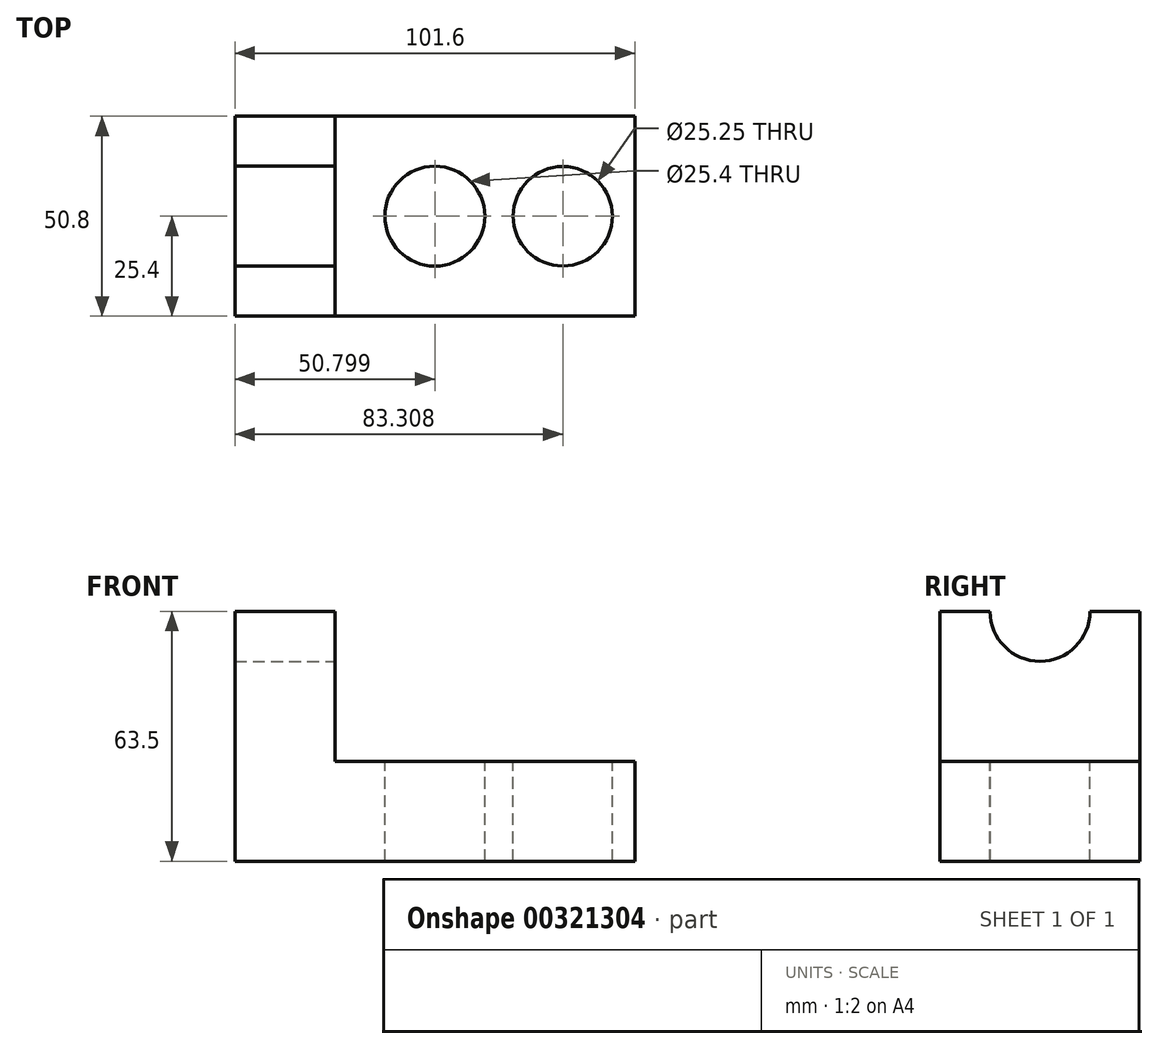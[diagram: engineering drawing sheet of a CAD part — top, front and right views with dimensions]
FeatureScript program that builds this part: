
annotation { "Feature Type Name" : "Feature", "Feature Type Description" : "" }
export const myFeature = defineFeature(function(context is Context, id is Id, definition is map)
    precondition{}
    {
        {
            var Q0;
            Q0=qCreatedBy(makeId("Front.planeOp"),FACE);
            var sketch = newSketch(context, id + "F0", { "sketchPlane" : qUnion([Q0])});
            skLineSegment(sketch, "E0", {"start": v(-43.87, 25.06) * mm, "end": v(-43.87, -38.44) * mm});
            skLineSegment(sketch, "E1", {"start": v(-43.87, -38.44) * mm, "end": v(57.73, -38.44) * mm});
            skLineSegment(sketch, "E2", {"start": v(57.73, -38.44) * mm, "end": v(57.73, -13.04) * mm});
            skLineSegment(sketch, "E3", {"start": v(-43.87, 25.06) * mm, "end": v(-18.47, 25.06) * mm});
            skLineSegment(sketch, "E4", {"start": v(57.73, -13.04) * mm, "end": v(-18.47, -13.04) * mm});
            skLineSegment(sketch, "E5", {"start": v(-18.47, -13.04) * mm, "end": v(-18.47, 25.06) * mm});
            skSolve(sketch);
        }
        {
            var Q0;
            Q0 = qSketchRegion(id + "F0", true);
            extrude(context, id + "F1", {"entities" : qUnion([Q0]), "depth" : 50.8 * mm});
        }
        {
            var Q0;
            Q0=makeQuery(id+"F1.opExtrude","SWEPT_FACE",FACE,{"disambiguationData":[OSD([sQuery(id+"F0.wireOp",EDGE,"E5")])]});
            var sketch = newSketch(context, id + "F2", { "sketchPlane" : qUnion([Q0])});
            skPoint(sketch, "E6.startSnap0", {"position": v(-25.4, -13.04) * mm});
            skPoint(sketch, "E6.endSnap0", {"position": v(-25.4, 25.06) * mm});
            skArc(sketch, "E7", {"start": v(-38.1, 25.06) * mm, "mid": v(-25.4, 12.36) * mm, "end": v(-12.7, 25.06) * mm});
            skLineSegment(sketch, "E8", {"start": v(-38.1, 25.06) * mm, "end": v(-12.7, 25.06) * mm});
            skSolve(sketch);
        }
        {
            var Q0;
            Q0=makeQuery(id+"F2.imprint","IMPRINT",FACE,{"disambiguationData":[TD([[makeQuery(id+"F2.imprint","IMPRINT",EDGE,{"derivedFrom":sQuery(id+"F2.wireOp",EDGE,"E7")}),1.0]])]});
            extrude(context, id + "F3", {"entities" : qUnion([Q0]), "operationType" : NewBodyOperationType.REMOVE, "oppositeDirection" : true, "depth" : 80.26 * mm});
        }
        {
            var Q0;
            Q0=makeQuery(id+"F1.opExtrude","SWEPT_FACE",FACE,{"disambiguationData":[OSD([sQuery(id+"F0.wireOp",EDGE,"E4")])]});
            var sketch = newSketch(context, id + "F4", { "sketchPlane" : qUnion([Q0])});
            skCircle(sketch, "E9", {"center": v(6.93, -25.4) * mm, "radius": 12.7 * mm});
            skPoint(sketch, "E9.centerSnap0", {"position": v(-18.47, -25.4) * mm});
            skLineSegment(sketch, "E10", {"start": v(-18.47, 0) * mm, "end": v(45.03, 0) * mm});
            skCircle(sketch, "E11", {"center": v(39.44, -25.4) * mm, "radius": 12.63 * mm});
            skSolve(sketch);
        }
        {
            var Q0;
            Q0 = qSketchRegion(id + "F4", true);
            extrude(context, id + "F5", {"entities" : qUnion([Q0]), "operationType" : NewBodyOperationType.REMOVE, "oppositeDirection" : true, "depth" : 50.8 * mm});
        }
    });
